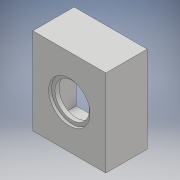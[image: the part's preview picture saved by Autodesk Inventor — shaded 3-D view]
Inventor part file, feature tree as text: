
AUTODESK INVENTOR PART (.ipt)
format: ipt  version: 2018 (Build 220112000, 112)  size: 117,760 bytes
history: native  units: mm
features: extrude x4, sketch x4
ambient origin geometry x8: Origin, YZ Plane, XZ Plane, XY Plane, X Axis, Y Axis, Z Axis, Center Point
bodies: Solid1 (feature_tree)
feature tree (8):
  extrude  "Extrusion1"  Depth=63.0mm
  extrude  "Extrusion2"  Depth=50.0mm
  extrude  "Extrusion3"  Depth=25.0mm TaperAngle=0.0deg
  extrude  "Extrusion4"  Depth=2.0mm TaperAngle=0.0deg
  sketch  "Sketch1"  dims[d0=53.0mm d1=63.0mm]
  sketch  "Sketch2"  dims[d2=30.0mm d3=0.0mm d4=50.0mm]
  sketch  "Sketch3"  dims[d5=60.0mm d6=25.0mm d7=0.0mm]
  sketch  "Sketch4"  dims[d10=30.0mm d11=2.0mm d12=0.0mm d13=25.0mm d14=2.0mm d15=0.0mm]
